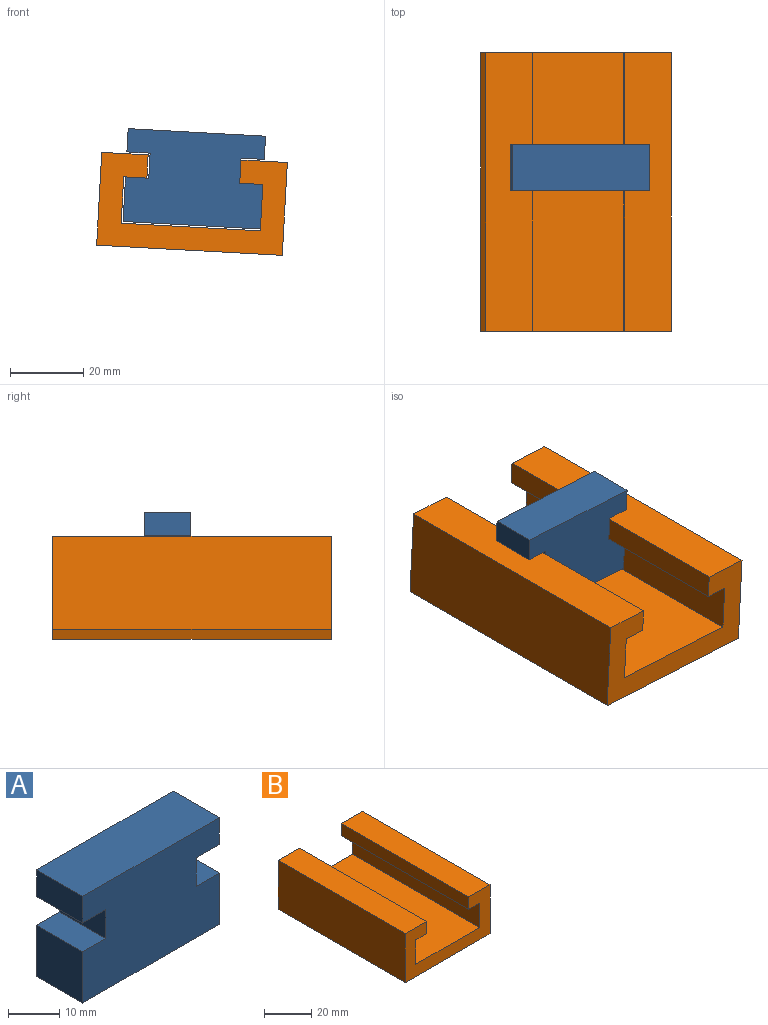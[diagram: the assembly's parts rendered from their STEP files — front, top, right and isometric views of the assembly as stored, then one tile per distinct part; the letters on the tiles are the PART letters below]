
ASSEMBLY  parts=2 mates=1
PART A: 14 faces, bbox 37.6x12.7x25.4 mm
  f0: plane 12.7x12.19mm, normal (-1,0,0), area 154.8mm2, adj f1,f11,f12,f13
  f1: plane 37.59x12.7mm, normal (0,0,-1), area 477.4mm2, adj f0,f2,f12,f13
  f2: plane 12.7x12.19mm, normal (1,0,0), area 154.8mm2, adj f1,f3,f12,f13
  f3: plane 12.7x6.35mm, normal (0,0,1), area 80.6mm2, adj f2,f4,f12,f13
  f4: plane 12.7x6.86mm, normal (1,0,0), area 87.1mm2, adj f3,f5,f12,f13
  f5: plane 12.7x6.35mm, normal (0,0,-1), area 80.6mm2, adj f4,f6,f12,f13
  f6: plane 12.7x6.35mm, normal (1,0,0), area 80.6mm2, adj f5,f7,f12,f13
  f7: plane 37.59x12.7mm, normal (0,0,1), area 477.4mm2, adj f6,f8,f12,f13
  f8: plane 12.7x6.35mm, normal (-1,0,0), area 80.6mm2, adj f7,f9,f12,f13
  f9: plane 12.7x6.35mm, normal (0,0,-1), area 80.6mm2, adj f8,f10,f12,f13
  f10: plane 12.7x6.86mm, normal (-1,0,0), area 87.1mm2, adj f9,f11,f12,f13
  f11: plane 12.7x6.35mm, normal (0,0,1), area 80.6mm2, adj f0,f10,f12,f13
  f12: plane 37.59x25.4mm, normal (0,-1,0), area 867.7mm2, adj f0,f1,f2,f3,f4,f5,f6,f7
  f13: plane 37.59x25.4mm, normal (0,1,0), area 867.7mm2, adj f0,f1,f2,f3,f4,f5,f6,f7
PART B: 14 faces, bbox 50.8x76.2x25.4 mm
  f0: plane 76.2x25.4mm, normal (-1,0,0), area 1935.5mm2, adj f1,f11,f12,f13
  f1: plane 76.2x50.8mm, normal (0,0,-1), area 3871mm2, adj f0,f2,f12,f13
  f2: plane 76.2x25.4mm, normal (1,0,0), area 1935.5mm2, adj f1,f3,f12,f13
  f3: plane 76.2x12.7mm, normal (0,0,1), area 967.7mm2, adj f2,f4,f12,f13
  f4: plane 76.2x6.35mm, normal (-1,0,0), area 483.9mm2, adj f3,f5,f12,f13
  f5: plane 76.2x6.35mm, normal (0,0,-1), area 483.9mm2, adj f4,f6,f12,f13
  f6: plane 76.2x12.7mm, normal (-1,0,0), area 967.7mm2, adj f5,f7,f12,f13
  f7: plane 76.2x38.1mm, normal (0,0,1), area 2903.2mm2, adj f6,f8,f12,f13
  f8: plane 76.2x12.7mm, normal (1,0,0), area 967.7mm2, adj f7,f9,f12,f13
  f9: plane 76.2x6.35mm, normal (0,0,-1), area 483.9mm2, adj f8,f10,f12,f13
  f10: plane 76.2x6.35mm, normal (1,0,0), area 483.9mm2, adj f9,f11,f12,f13
  f11: plane 76.2x12.7mm, normal (0,0,1), area 967.7mm2, adj f0,f10,f12,f13
  f12: plane 50.8x25.4mm, normal (0,-1,0), area 645.2mm2, adj f0,f1,f2,f3,f4,f5,f6,f7
  f13: plane 50.8x25.4mm, normal (0,1,0), area 645.2mm2, adj f0,f1,f2,f3,f4,f5,f6,f7
PLACE A rot(axis=(0,1,0),3.1deg) t=(35.83,-44.29,38.74)mm
PLACE B rot(axis=(0,1,0),3.1deg) t=(35.56,-19.25,38.5)mm fixed
MATE slider B.f12 <-> A.f12  axis (0,-1,0) through (74.65,-95.45,55.44)mm
